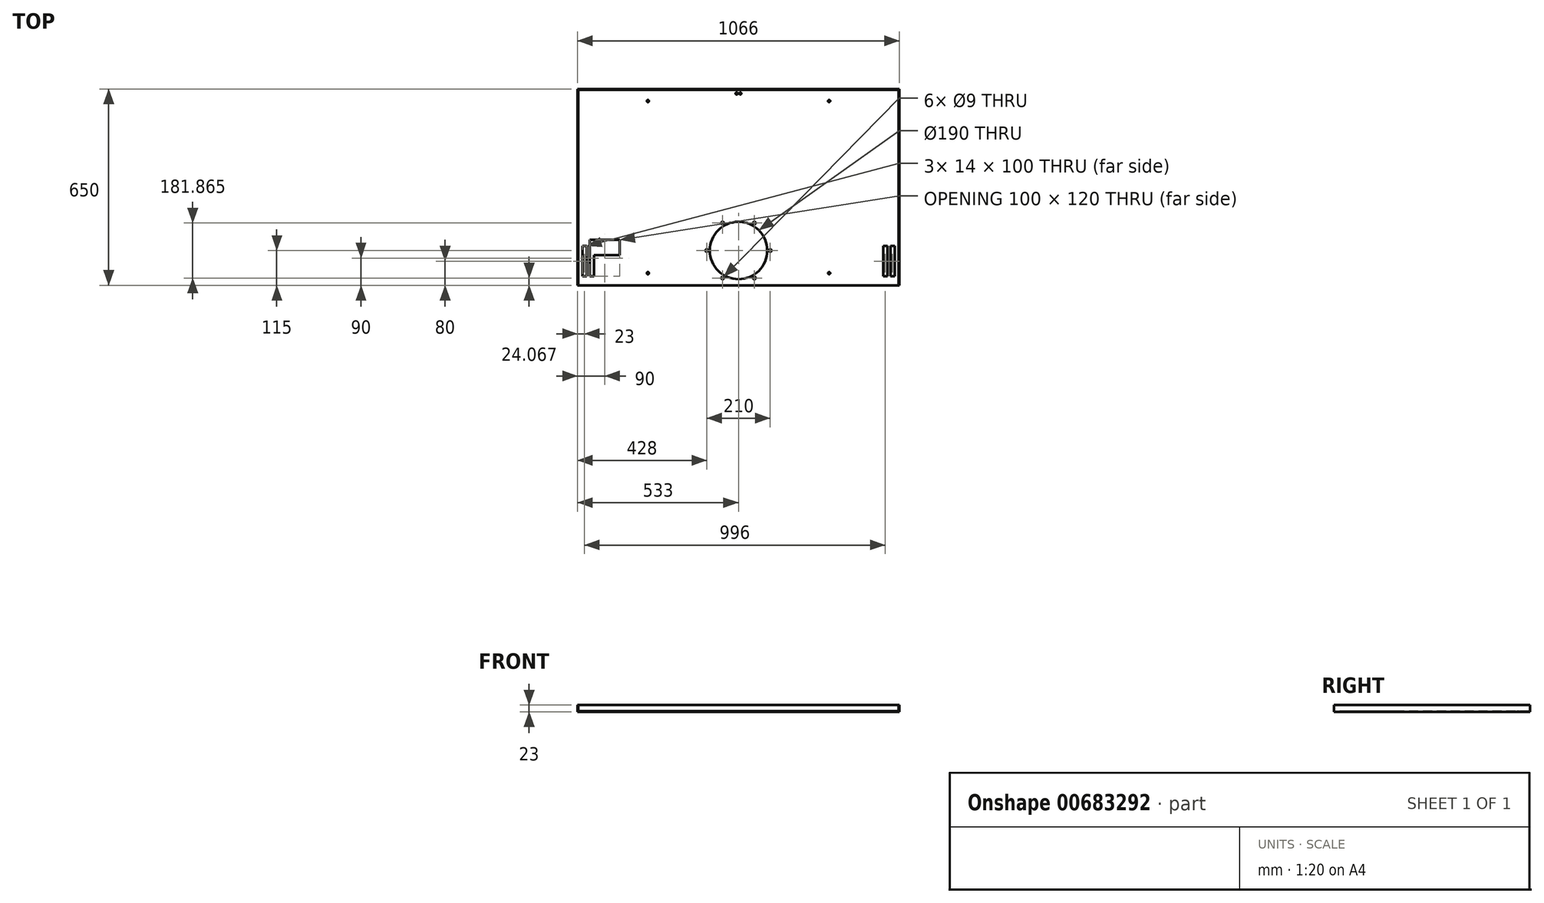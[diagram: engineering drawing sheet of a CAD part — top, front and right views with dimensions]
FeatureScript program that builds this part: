
annotation { "Feature Type Name" : "Feature", "Feature Type Description" : "" }
export const myFeature = defineFeature(function(context is Context, id is Id, definition is map)
    precondition{}
    {
        {
            var Q0;
            Q0=qCreatedBy(makeId("Top.planeOp"),FACE);
            var sketch = newSketch(context, id + "F0", { "sketchPlane" : qUnion([Q0])});
            skLineSegment(sketch, "E0.bottom", {"start": v(533, 325) * mm, "end": v(-533, 325) * mm});
            skLineSegment(sketch, "E0.top", {"start": v(533, -325) * mm, "end": v(-533, -325) * mm});
            skLineSegment(sketch, "E0.left", {"start": v(533, 325) * mm, "end": v(533, -325) * mm});
            skLineSegment(sketch, "E0.right", {"start": v(-533, 325) * mm, "end": v(-533, -325) * mm});
            skPoint(sketch, "E0.middle", {"position": v(0, 0) * mm});
            skCircle(sketch, "E1", {"center": v(0, -210) * mm, "radius": 95 * mm});
            skCircle(sketch, "E2", {"center": v(0, -210) * mm, "radius": 105 * mm, "construction": true});
            skCircle(sketch, "E3", {"center": v(-105, -210) * mm, "radius": 4.5 * mm});
            skCircle(sketch, "E4", {"center": v(105, -210) * mm, "radius": 4.5 * mm});
            skCircle(sketch, "E5", {"center": v(52.5, -119.07) * mm, "radius": 4.5 * mm});
            skCircle(sketch, "E6", {"center": v(-52.5, -119.07) * mm, "radius": 4.5 * mm});
            skCircle(sketch, "E7", {"center": v(-52.5, -300.93) * mm, "radius": 4.5 * mm});
            skLineSegment(sketch, "E8", {"start": v(0, -210) * mm, "end": v(-52.5, -119.07) * mm, "construction": true});
            skLineSegment(sketch, "E9", {"start": v(0, -210) * mm, "end": v(52.5, -119.07) * mm, "construction": true});
            skLineSegment(sketch, "E10", {"start": v(0, -210) * mm, "end": v(105, -210) * mm, "construction": true});
            skLineSegment(sketch, "E11", {"start": v(0, -210) * mm, "end": v(-105, -210) * mm, "construction": true});
            skLineSegment(sketch, "E12", {"start": v(0, -210) * mm, "end": v(-52.5, -300.93) * mm, "construction": true});
            skCircle(sketch, "E13", {"center": v(52.5, -300.93) * mm, "radius": 4.5 * mm});
            skLineSegment(sketch, "E14", {"start": v(0, -210) * mm, "end": v(52.5, -300.93) * mm, "construction": true});
            skLineSegment(sketch, "E15", {"start": v(-580.65, -285) * mm, "end": v(608.61, -285) * mm, "construction": true});
            skLineSegment(sketch, "E16", {"start": v(300, 378.16) * mm, "end": v(300, -434.44) * mm, "construction": true});
            skCircle(sketch, "E17", {"center": v(300, -285) * mm, "radius": 3.5 * mm});
            skLineSegment(sketch, "E18", {"start": v(-300, 400.12) * mm, "end": v(-300, -442.88) * mm, "construction": true});
            skCircle(sketch, "E19", {"center": v(-300, -285) * mm, "radius": 3.5 * mm});
            skLineSegment(sketch, "E20", {"start": v(510, 382.3) * mm, "end": v(510, -395.76) * mm, "construction": true});
            skLineSegment(sketch, "E21", {"start": v(-586.04, -195) * mm, "end": v(614.07, -195) * mm, "construction": true});
            skLineSegment(sketch, "E22", {"start": v(503, 381.91) * mm, "end": v(503, -394.73) * mm, "construction": true});
            skLineSegment(sketch, "E23", {"start": v(517, 381.91) * mm, "end": v(517, -395.44) * mm, "construction": true});
            skLineSegment(sketch, "E24", {"start": v(0, 378.02) * mm, "end": v(0, -373.85) * mm, "construction": true});
            skLineSegment(sketch, "E25.MirrorCS", {"start": v(-503, 381.91) * mm, "end": v(-503, -394.73) * mm, "construction": true});
            skLineSegment(sketch, "E26.MirrorCS", {"start": v(-510, 382.3) * mm, "end": v(-510, -395.76) * mm, "construction": true});
            skLineSegment(sketch, "E27.MirrorCS", {"start": v(-517, 381.91) * mm, "end": v(-517, -395.44) * mm, "construction": true});
            skLineSegment(sketch, "E28", {"start": v(503, -195) * mm, "end": v(517, -195) * mm});
            skLineSegment(sketch, "E29", {"start": v(517, -195) * mm, "end": v(517, -325) * mm});
            skLineSegment(sketch, "E30", {"start": v(503, -195) * mm, "end": v(503, -325) * mm});
            skLineSegment(sketch, "E31", {"start": v(-517, -195) * mm, "end": v(-503, -195) * mm});
            skLineSegment(sketch, "E32", {"start": v(-503, -195) * mm, "end": v(-503, -325) * mm});
            skLineSegment(sketch, "E33", {"start": v(-517, -195) * mm, "end": v(-517, -325) * mm});
            skLineSegment(sketch, "E34", {"start": v(-664.26, 310) * mm, "end": v(640.07, 310) * mm, "construction": true});
            skLineSegment(sketch, "E35", {"start": v(-6, 374.97) * mm, "end": v(-6, -374.59) * mm, "construction": true});
            skLineSegment(sketch, "E36", {"start": v(6, 377.22) * mm, "end": v(6, -376.61) * mm, "construction": true});
            skCircle(sketch, "E37", {"center": v(-6, 310) * mm, "radius": 3.5 * mm});
            skCircle(sketch, "E38", {"center": v(6, 310) * mm, "radius": 3.5 * mm});
            skLineSegment(sketch, "E39", {"start": v(-685.25, 285) * mm, "end": v(727.74, 285) * mm, "construction": true});
            skCircle(sketch, "E40", {"center": v(300, 285) * mm, "radius": 3.5 * mm});
            skCircle(sketch, "E41", {"center": v(-300, 285) * mm, "radius": 3.5 * mm});
            skLineSegment(sketch, "E42", {"start": v(-593.9, -210) * mm, "end": v(628.34, -210) * mm, "construction": true});
            skLineSegment(sketch, "E43", {"start": v(-493, 354.73) * mm, "end": v(-493, -170) * mm, "construction": true});
            skLineSegment(sketch, "E44.left", {"start": v(-493, -170) * mm, "end": v(-493, -219.68) * mm, "construction": true});
            skLineSegment(sketch, "E45.trimOffspring", {"start": v(-493, -219.68) * mm, "end": v(-493, -359.34) * mm, "construction": true});
            skPoint(sketch, "E46.third.point", {"position": v(-493, -210) * mm});
            skLineSegment(sketch, "E47", {"start": v(-573.33, -175) * mm, "end": v(-338.02, -175) * mm, "construction": true});
            skLineSegment(sketch, "E48", {"start": v(-574.53, -225) * mm, "end": v(-337.62, -225) * mm, "construction": true});
            skPoint(sketch, "E49.first.point", {"position": v(-468, -175) * mm});
            skPoint(sketch, "E49.second.point", {"position": v(-468, -225) * mm});
            skPoint(sketch, "E50.first.point", {"position": v(-418, -175) * mm});
            skPoint(sketch, "E50.second.point", {"position": v(-418, -225) * mm});
            skPoint(sketch, "E50.third.point", {"position": v(-443, -210) * mm});
            skLineSegment(sketch, "E51", {"start": v(-468, -175) * mm, "end": v(-418, -175) * mm});
            skLineSegment(sketch, "E52", {"start": v(-468, -225) * mm, "end": v(-418, -225) * mm});
            skLineSegment(sketch, "E53", {"start": v(-517, -295) * mm, "end": v(-503, -295) * mm});
            skLineSegment(sketch, "E54.MirrorCS", {"start": v(517, -295) * mm, "end": v(503, -295) * mm});
            skLineSegment(sketch, "E55", {"start": v(-468, -175) * mm, "end": v(-493, -175) * mm});
            skLineSegment(sketch, "E56", {"start": v(-493, -175) * mm, "end": v(-493, -225) * mm});
            skLineSegment(sketch, "E57", {"start": v(-493, -225) * mm, "end": v(-468, -225) * mm});
            skLineSegment(sketch, "E58", {"start": v(-418, -175) * mm, "end": v(-393, -175) * mm});
            skPoint(sketch, "E58.endSnap0", {"position": v(-393, -200) * mm});
            skLineSegment(sketch, "E59", {"start": v(-393, -175) * mm, "end": v(-393, -225) * mm});
            skLineSegment(sketch, "E60", {"start": v(-393, -225) * mm, "end": v(-418, -225) * mm});
            skSolve(sketch);
        }
        {
            var Q0;
            Q0=makeQuery(id+"F0.imprint","IMPRINT",FACE,{"disambiguationData":[TD([[makeQuery(id+"F0.imprint","IMPRINT",EDGE,{"derivedFrom":sQuery(id+"F0.wireOp",EDGE,"E0.bottom")}),1.0]])]});
            var Q1;
            {var subQ5=sQuery(id+"F0.wireOp",EDGE,"E53");Q1=makeQuery(id+"F0.imprint","IMPRINT",FACE,{"disambiguationData":[TD([[makeQuery(id+"F0.imprint","IMPRINT",EDGE,{"derivedFrom":subQ5}),-1.0]])]});}
            var Q2;
            {var subQ5=sQuery(id+"F0.wireOp",EDGE,"E54.MirrorCS");Q2=makeQuery(id+"F0.imprint","IMPRINT",FACE,{"disambiguationData":[TD([[makeQuery(id+"F0.imprint","IMPRINT",EDGE,{"derivedFrom":subQ5}),1.0]])]});}
            extrude(context, id + "F1", {"entities" : qUnion([Q0, Q1, Q2]), "oppositeDirection" : true, "depth" : 3 * mm, "offsetDistance" : 25 * mm});
        }
        {
            var Q0;
            Q0=makeQuery(id+"F1.opExtrude","CAP_FACE",FACE,{"disambiguationData":[OSD([sQuery(id+"F0.wireOp",EDGE,"E0.bottom"),sQuery(id+"F0.wireOp",EDGE,"E0.top"),sQuery(id+"F0.wireOp",EDGE,"E0.left"),sQuery(id+"F0.wireOp",EDGE,"E0.right"),sQuery(id+"F0.wireOp",EDGE,"E1"),sQuery(id+"F0.wireOp",EDGE,"E3"),sQuery(id+"F0.wireOp",EDGE,"E4"),sQuery(id+"F0.wireOp",EDGE,"E5"),sQuery(id+"F0.wireOp",EDGE,"E6"),sQuery(id+"F0.wireOp",EDGE,"E7"),sQuery(id+"F0.wireOp",EDGE,"E13"),sQuery(id+"F0.wireOp",EDGE,"E17"),sQuery(id+"F0.wireOp",EDGE,"E19"),sQuery(id+"F0.wireOp",EDGE,"E28"),sQuery(id+"F0.wireOp",EDGE,"E29"),sQuery(id+"F0.wireOp",EDGE,"E30"),sQuery(id+"F0.wireOp",EDGE,"E31"),sQuery(id+"F0.wireOp",EDGE,"E32"),sQuery(id+"F0.wireOp",EDGE,"E33"),sQuery(id+"F0.wireOp",EDGE,"E37"),sQuery(id+"F0.wireOp",EDGE,"E38")])],"isStart":true});
            var sketch = newSketch(context, id + "F2", { "sketchPlane" : qUnion([Q0])});
            skLineSegment(sketch, "E61", {"start": v(-530, -325) * mm, "end": v(-530, 322) * mm});
            skLineSegment(sketch, "E62", {"start": v(-530, 322) * mm, "end": v(530, 322) * mm});
            skLineSegment(sketch, "E63", {"start": v(530, 322) * mm, "end": v(530, -325) * mm});
            skSolve(sketch);
        }
        {
            var Q0;
            {var subQ5=sQuery(id+"F2.wireOp",EDGE,"E61");Q0=makeQuery(id+"F2.imprint","IMPRINT",FACE,{"disambiguationData":[TD([[makeQuery(id+"F2.imprint","IMPRINT",EDGE,{"derivedFrom":subQ5}),1.0]])]});}
            extrude(context, id + "F3", {"entities" : qUnion([Q0]), "operationType" : NewBodyOperationType.ADD, "depth" : 20 * mm, "offsetDistance" : 25 * mm});
        }
        {
            var Q0;
            Q0=makeQuery(id+"F1.opExtrude","CAP_FACE",FACE,{"disambiguationData":[OSD([sQuery(id+"F0.wireOp",EDGE,"E0.bottom"),sQuery(id+"F0.wireOp",EDGE,"E0.top"),sQuery(id+"F0.wireOp",EDGE,"E0.left"),sQuery(id+"F0.wireOp",EDGE,"E0.right"),sQuery(id+"F0.wireOp",EDGE,"E1"),sQuery(id+"F0.wireOp",EDGE,"E3"),sQuery(id+"F0.wireOp",EDGE,"E4"),sQuery(id+"F0.wireOp",EDGE,"E5"),sQuery(id+"F0.wireOp",EDGE,"E6"),sQuery(id+"F0.wireOp",EDGE,"E7"),sQuery(id+"F0.wireOp",EDGE,"E13"),sQuery(id+"F0.wireOp",EDGE,"E17"),sQuery(id+"F0.wireOp",EDGE,"E19"),sQuery(id+"F0.wireOp",EDGE,"E28"),sQuery(id+"F0.wireOp",EDGE,"E29"),sQuery(id+"F0.wireOp",EDGE,"E30"),sQuery(id+"F0.wireOp",EDGE,"E31"),sQuery(id+"F0.wireOp",EDGE,"E32"),sQuery(id+"F0.wireOp",EDGE,"E33"),sQuery(id+"F0.wireOp",EDGE,"E37"),sQuery(id+"F0.wireOp",EDGE,"E38"),sQuery(id+"F0.wireOp",EDGE,"E40"),sQuery(id+"F0.wireOp",EDGE,"E41"),sQuery(id+"F0.wireOp",EDGE,"E51"),sQuery(id+"F0.wireOp",EDGE,"E52"),sQuery(id+"F0.wireOp",EDGE,"E53"),sQuery(id+"F0.wireOp",EDGE,"E54.MirrorCS"),sQuery(id+"F0.wireOp",EDGE,"E55"),sQuery(id+"F0.wireOp",EDGE,"E56"),sQuery(id+"F0.wireOp",EDGE,"E57"),sQuery(id+"F0.wireOp",EDGE,"E58"),sQuery(id+"F0.wireOp",EDGE,"E59"),sQuery(id+"F0.wireOp",EDGE,"E60")])],"isStart":true});
            var sketch = newSketch(context, id + "F4", { "sketchPlane" : qUnion([Q0])});
            skLineSegment(sketch, "E64", {"start": v(0, 266.76) * mm, "end": v(0, -422.87) * mm, "construction": true});
            skLineSegment(sketch, "E65.bottom", {"start": v(-493, -195) * mm, "end": v(-479, -195) * mm});
            skLineSegment(sketch, "E65.top", {"start": v(-493, -295) * mm, "end": v(-479, -295) * mm});
            skLineSegment(sketch, "E65.left", {"start": v(-493, -195) * mm, "end": v(-493, -295) * mm});
            skLineSegment(sketch, "E65.right", {"start": v(-479, -195) * mm, "end": v(-479, -295) * mm});
            skLineSegment(sketch, "E66.MirrorCS", {"start": v(479, -195) * mm, "end": v(479, -295) * mm});
            skLineSegment(sketch, "E67.MirrorCS", {"start": v(493, -195) * mm, "end": v(479, -195) * mm});
            skLineSegment(sketch, "E68.MirrorCS", {"start": v(493, -195) * mm, "end": v(493, -295) * mm});
            skLineSegment(sketch, "E69.MirrorCS", {"start": v(493, -295) * mm, "end": v(479, -295) * mm});
            skSolve(sketch);
        }
        {
            var Q0;
            {var subQ0=sQuery(id+"F4.wireOp",EDGE,"E65.top");Q0=makeQuery(id+"F4.imprint","IMPRINT",FACE,{"disambiguationData":[TD([[makeQuery(id+"F4.imprint","IMPRINT",EDGE,{"derivedFrom":subQ0}),1.0]])]});}
            var Q1;
            Q1=makeQuery(id+"F4.imprint","IMPRINT",FACE,{"disambiguationData":[TD([[makeQuery(id+"F4.imprint","IMPRINT",EDGE,{"derivedFrom":sQuery(id+"F4.wireOp",EDGE,"E66.MirrorCS")}),1.0]])]});
            extrude(context, id + "F5", {"entities" : qUnion([Q0, Q1]), "operationType" : NewBodyOperationType.REMOVE, "endBound" : BoundingType.THROUGH_ALL, "oppositeDirection" : true, "depth" : 25 * mm, "offsetDistance" : 25 * mm});
        }
    });
